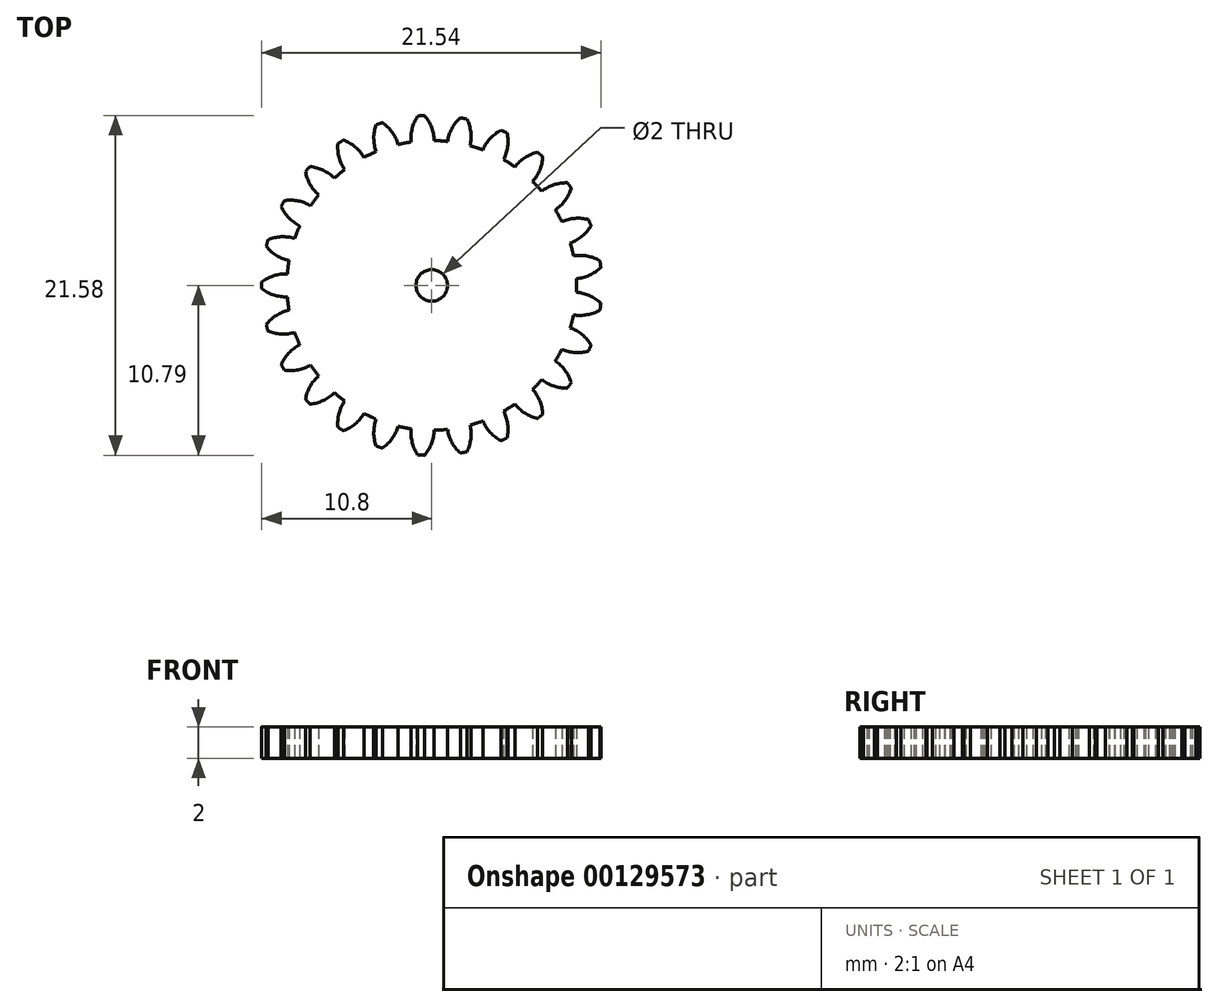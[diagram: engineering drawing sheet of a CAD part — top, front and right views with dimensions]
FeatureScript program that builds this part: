
annotation { "Feature Type Name" : "Feature", "Feature Type Description" : "" }
export const myFeature = defineFeature(function(context is Context, id is Id, definition is map)
    precondition{}
    {
        {
            var Q0;
            Q0=qCreatedBy(makeId("Top.planeOp"),FACE);
            var sketch = newSketch(context, id + "F0", { "sketchPlane" : qUnion([Q0])});
            skCircle(sketch, "E0", {"center": v(0, 0) * mm, "radius": 9.2 * mm, "construction": true});
            skCircle(sketch, "E1", {"center": v(0, 0) * mm, "radius": 10 * mm, "construction": true});
            skCircle(sketch, "E2", {"center": v(0, 0) * mm, "radius": 10.8 * mm, "construction": true});
            skLineSegment(sketch, "E3", {"start": v(0, 0) * mm, "end": v(0, 14.58) * mm, "construction": true});
            skLineSegment(sketch, "E4", {"start": v(0, 0) * mm, "end": v(-0.92, 14.56) * mm, "construction": true});
            skLineSegment(sketch, "E5", {"start": v(0, 10) * mm, "end": v(-10.54, 10) * mm, "construction": true});
            skLineSegment(sketch, "E6", {"start": v(0, 10) * mm, "end": v(-7.33, 7.33) * mm, "construction": true});
            skCircle(sketch, "E7", {"center": v(0, 10) * mm, "radius": 2.5 * mm, "construction": true});
            skCircle(sketch, "E8", {"center": v(-2.35, 9.14) * mm, "radius": 2.5 * mm, "construction": true});
            skArc(sketch, "E9", {"start": v(-4.7, 10) * mm, "mid": v(-4.75, 9.84) * mm, "end": v(-4.8, 9.68) * mm});
            skPoint(sketch, "E10.center", {"position": v(4.35, 4.65) * mm});
            skCircle(sketch, "E11", {"center": v(0, 0) * mm, "radius": 1 * mm});
            skArc(sketch, "E12", {"start": v(0.15, 9.2) * mm, "mid": v(-0.02, 10.05) * mm, "end": v(-0.47, 10.79) * mm});
            skArc(sketch, "E13.MirrorCS", {"start": v(-1.3, 9.1) * mm, "mid": v(-1.24, 9.97) * mm, "end": v(-0.89, 10.76) * mm});
            skArc(sketch, "E14", {"start": v(-0.47, 10.79) * mm, "mid": v(-0.68, 10.78) * mm, "end": v(-0.89, 10.76) * mm});
            skArc(sketch, "E15.1.0", {"start": v(-3.14, 10.33) * mm, "mid": v(-3.34, 10.27) * mm, "end": v(-3.54, 10.2) * mm});
            skArc(sketch, "E15.1.1", {"start": v(-2.14, 8.95) * mm, "mid": v(-2.52, 9.73) * mm, "end": v(-3.14, 10.33) * mm});
            skArc(sketch, "E15.1.2", {"start": v(-3.53, 8.5) * mm, "mid": v(-3.68, 9.35) * mm, "end": v(-3.54, 10.2) * mm});
            skArc(sketch, "E15.2.0", {"start": v(-5.6, 9.23) * mm, "mid": v(-5.79, 9.12) * mm, "end": v(-5.96, 9) * mm});
            skArc(sketch, "E15.2.1", {"start": v(-4.3, 8.13) * mm, "mid": v(-4.86, 8.8) * mm, "end": v(-5.6, 9.23) * mm});
            skArc(sketch, "E15.2.2", {"start": v(-5.53, 7.35) * mm, "mid": v(-5.9, 8.14) * mm, "end": v(-5.96, 9) * mm});
            skArc(sketch, "E15.3.0", {"start": v(-7.73, 7.55) * mm, "mid": v(-7.87, 7.4) * mm, "end": v(-8.02, 7.24) * mm});
            skArc(sketch, "E15.3.1", {"start": v(-6.19, 6.8) * mm, "mid": v(-6.9, 7.31) * mm, "end": v(-7.73, 7.55) * mm});
            skArc(sketch, "E15.3.2", {"start": v(-7.18, 5.75) * mm, "mid": v(-7.73, 6.42) * mm, "end": v(-8.02, 7.24) * mm});
            skArc(sketch, "E15.4.0", {"start": v(-9.36, 5.39) * mm, "mid": v(-9.46, 5.2) * mm, "end": v(-9.56, 5.02) * mm});
            skArc(sketch, "E15.4.1", {"start": v(-7.69, 5.06) * mm, "mid": v(-8.5, 5.37) * mm, "end": v(-9.36, 5.39) * mm});
            skArc(sketch, "E15.4.2", {"start": v(-8.39, 3.78) * mm, "mid": v(-9.08, 4.3) * mm, "end": v(-9.56, 5.02) * mm});
            skArc(sketch, "E15.5.0", {"start": v(-10.4, 2.9) * mm, "mid": v(-10.46, 2.69) * mm, "end": v(-10.51, 2.48) * mm});
            skArc(sketch, "E15.5.1", {"start": v(-8.7, 2.99) * mm, "mid": v(-9.56, 3.09) * mm, "end": v(-10.4, 2.9) * mm});
            skArc(sketch, "E15.5.2", {"start": v(-9.06, 1.58) * mm, "mid": v(-9.87, 1.9) * mm, "end": v(-10.51, 2.48) * mm});
            skArc(sketch, "E15.6.0", {"start": v(-10.8, 0.21) * mm, "mid": v(-10.8, 0) * mm, "end": v(-10.8, -0.21) * mm});
            skArc(sketch, "E15.6.1", {"start": v(-9.17, 0.73) * mm, "mid": v(-10.03, 0.61) * mm, "end": v(-10.8, 0.21) * mm});
            skArc(sketch, "E15.6.2", {"start": v(-9.17, -0.73) * mm, "mid": v(-10.03, -0.61) * mm, "end": v(-10.8, -0.21) * mm});
            skArc(sketch, "E15.7.0", {"start": v(-10.51, -2.48) * mm, "mid": v(-10.46, -2.69) * mm, "end": v(-10.4, -2.9) * mm});
            skArc(sketch, "E15.7.1", {"start": v(-9.06, -1.58) * mm, "mid": v(-9.87, -1.9) * mm, "end": v(-10.51, -2.48) * mm});
            skArc(sketch, "E15.7.2", {"start": v(-8.7, -2.99) * mm, "mid": v(-9.56, -3.09) * mm, "end": v(-10.4, -2.9) * mm});
            skArc(sketch, "E15.8.0", {"start": v(-9.56, -5.02) * mm, "mid": v(-9.46, -5.2) * mm, "end": v(-9.36, -5.39) * mm});
            skArc(sketch, "E15.8.1", {"start": v(-8.39, -3.78) * mm, "mid": v(-9.08, -4.3) * mm, "end": v(-9.56, -5.02) * mm});
            skArc(sketch, "E15.8.2", {"start": v(-7.69, -5.06) * mm, "mid": v(-8.5, -5.37) * mm, "end": v(-9.36, -5.39) * mm});
            skArc(sketch, "E15.9.0", {"start": v(-8.02, -7.24) * mm, "mid": v(-7.87, -7.4) * mm, "end": v(-7.73, -7.55) * mm});
            skArc(sketch, "E15.9.1", {"start": v(-7.18, -5.75) * mm, "mid": v(-7.73, -6.42) * mm, "end": v(-8.02, -7.24) * mm});
            skArc(sketch, "E15.9.2", {"start": v(-6.19, -6.8) * mm, "mid": v(-6.9, -7.31) * mm, "end": v(-7.73, -7.55) * mm});
            skArc(sketch, "E15.10.0", {"start": v(-5.96, -9) * mm, "mid": v(-5.79, -9.12) * mm, "end": v(-5.6, -9.23) * mm});
            skArc(sketch, "E15.10.1", {"start": v(-5.53, -7.35) * mm, "mid": v(-5.9, -8.14) * mm, "end": v(-5.96, -9) * mm});
            skArc(sketch, "E15.10.2", {"start": v(-4.3, -8.13) * mm, "mid": v(-4.86, -8.8) * mm, "end": v(-5.6, -9.23) * mm});
            skArc(sketch, "E15.11.0", {"start": v(-3.54, -10.2) * mm, "mid": v(-3.34, -10.27) * mm, "end": v(-3.14, -10.33) * mm});
            skArc(sketch, "E15.11.1", {"start": v(-3.53, -8.5) * mm, "mid": v(-3.68, -9.35) * mm, "end": v(-3.54, -10.2) * mm});
            skArc(sketch, "E15.11.2", {"start": v(-2.14, -8.95) * mm, "mid": v(-2.52, -9.73) * mm, "end": v(-3.14, -10.33) * mm});
            skArc(sketch, "E15.12.0", {"start": v(-0.89, -10.76) * mm, "mid": v(-0.68, -10.78) * mm, "end": v(-0.47, -10.79) * mm});
            skArc(sketch, "E15.12.1", {"start": v(-1.3, -9.1) * mm, "mid": v(-1.24, -9.97) * mm, "end": v(-0.89, -10.76) * mm});
            skArc(sketch, "E15.12.2", {"start": v(0.15, -9.2) * mm, "mid": v(-0.02, -10.05) * mm, "end": v(-0.47, -10.79) * mm});
            skArc(sketch, "E15.13.0", {"start": v(1.82, -10.65) * mm, "mid": v(2.02, -10.6) * mm, "end": v(2.23, -10.57) * mm});
            skArc(sketch, "E15.13.1", {"start": v(1, -9.15) * mm, "mid": v(1.28, -9.97) * mm, "end": v(1.82, -10.65) * mm});
            skArc(sketch, "E15.13.2", {"start": v(2.43, -8.87) * mm, "mid": v(2.48, -9.74) * mm, "end": v(2.23, -10.57) * mm});
            skArc(sketch, "E15.14.0", {"start": v(4.4, -9.86) * mm, "mid": v(4.6, -9.77) * mm, "end": v(4.79, -9.68) * mm});
            skArc(sketch, "E15.14.1", {"start": v(3.25, -8.6) * mm, "mid": v(3.72, -9.34) * mm, "end": v(4.4, -9.86) * mm});
            skArc(sketch, "E15.14.2", {"start": v(4.56, -7.99) * mm, "mid": v(4.82, -8.81) * mm, "end": v(4.79, -9.68) * mm});
            skArc(sketch, "E15.15.0", {"start": v(6.72, -8.45) * mm, "mid": v(6.88, -8.32) * mm, "end": v(7.05, -8.18) * mm});
            skArc(sketch, "E15.15.1", {"start": v(5.29, -7.53) * mm, "mid": v(5.92, -8.12) * mm, "end": v(6.72, -8.45) * mm});
            skArc(sketch, "E15.15.2", {"start": v(6.4, -6.6) * mm, "mid": v(6.87, -7.34) * mm, "end": v(7.05, -8.18) * mm});
            skArc(sketch, "E15.16.0", {"start": v(8.61, -6.52) * mm, "mid": v(8.74, -6.35) * mm, "end": v(8.86, -6.18) * mm});
            skArc(sketch, "E15.16.1", {"start": v(7, -5.98) * mm, "mid": v(7.75, -6.4) * mm, "end": v(8.61, -6.52) * mm});
            skArc(sketch, "E15.16.2", {"start": v(7.85, -4.8) * mm, "mid": v(8.47, -5.4) * mm, "end": v(8.86, -6.18) * mm});
            skArc(sketch, "E15.17.0", {"start": v(9.96, -4.17) * mm, "mid": v(10.04, -3.98) * mm, "end": v(10.12, -3.78) * mm});
            skArc(sketch, "E15.17.1", {"start": v(8.26, -4.05) * mm, "mid": v(9.1, -4.26) * mm, "end": v(9.96, -4.17) * mm});
            skArc(sketch, "E15.17.2", {"start": v(8.8, -2.7) * mm, "mid": v(9.55, -3.12) * mm, "end": v(10.12, -3.78) * mm});
            skArc(sketch, "E15.18.0", {"start": v(10.69, -1.56) * mm, "mid": v(10.71, -1.35) * mm, "end": v(10.74, -1.14) * mm});
            skArc(sketch, "E15.18.1", {"start": v(9, -1.87) * mm, "mid": v(9.87, -1.86) * mm, "end": v(10.69, -1.56) * mm});
            skArc(sketch, "E15.18.2", {"start": v(9.2, -0.43) * mm, "mid": v(10.03, -0.65) * mm, "end": v(10.74, -1.14) * mm});
            skArc(sketch, "E15.19.0", {"start": v(10.74, 1.14) * mm, "mid": v(10.71, 1.35) * mm, "end": v(10.69, 1.56) * mm});
            skArc(sketch, "E15.19.1", {"start": v(9.2, 0.43) * mm, "mid": v(10.03, 0.65) * mm, "end": v(10.74, 1.14) * mm});
            skArc(sketch, "E15.19.2", {"start": v(9, 1.87) * mm, "mid": v(9.87, 1.86) * mm, "end": v(10.69, 1.56) * mm});
            skArc(sketch, "E15.20.0", {"start": v(10.12, 3.78) * mm, "mid": v(10.04, 3.98) * mm, "end": v(9.96, 4.17) * mm});
            skArc(sketch, "E15.20.1", {"start": v(8.8, 2.7) * mm, "mid": v(9.55, 3.12) * mm, "end": v(10.12, 3.78) * mm});
            skArc(sketch, "E15.20.2", {"start": v(8.26, 4.05) * mm, "mid": v(9.1, 4.26) * mm, "end": v(9.96, 4.17) * mm});
            skArc(sketch, "E15.21.0", {"start": v(8.86, 6.18) * mm, "mid": v(8.74, 6.35) * mm, "end": v(8.61, 6.52) * mm});
            skArc(sketch, "E15.21.1", {"start": v(7.85, 4.8) * mm, "mid": v(8.47, 5.4) * mm, "end": v(8.86, 6.18) * mm});
            skArc(sketch, "E15.21.2", {"start": v(7, 5.98) * mm, "mid": v(7.75, 6.4) * mm, "end": v(8.61, 6.52) * mm});
            skArc(sketch, "E15.22.0", {"start": v(7.05, 8.18) * mm, "mid": v(6.88, 8.32) * mm, "end": v(6.72, 8.45) * mm});
            skArc(sketch, "E15.22.1", {"start": v(6.4, 6.6) * mm, "mid": v(6.87, 7.34) * mm, "end": v(7.05, 8.18) * mm});
            skArc(sketch, "E15.22.2", {"start": v(5.29, 7.53) * mm, "mid": v(5.92, 8.12) * mm, "end": v(6.72, 8.45) * mm});
            skArc(sketch, "E15.23.0", {"start": v(4.79, 9.68) * mm, "mid": v(4.6, 9.77) * mm, "end": v(4.4, 9.86) * mm});
            skArc(sketch, "E15.23.1", {"start": v(4.56, 7.99) * mm, "mid": v(4.82, 8.81) * mm, "end": v(4.79, 9.68) * mm});
            skArc(sketch, "E15.23.2", {"start": v(3.25, 8.6) * mm, "mid": v(3.72, 9.34) * mm, "end": v(4.4, 9.86) * mm});
            skArc(sketch, "E15.24.0", {"start": v(2.23, 10.57) * mm, "mid": v(2.02, 10.6) * mm, "end": v(1.82, 10.65) * mm});
            skArc(sketch, "E15.24.1", {"start": v(2.43, 8.87) * mm, "mid": v(2.48, 9.74) * mm, "end": v(2.23, 10.57) * mm});
            skArc(sketch, "E15.24.2", {"start": v(1, 9.15) * mm, "mid": v(1.28, 9.97) * mm, "end": v(1.82, 10.65) * mm});
            skArc(sketch, "E16", {"start": v(1, 9.15) * mm, "mid": v(0.58, 9.18) * mm, "end": v(0.15, 9.2) * mm});
            skArc(sketch, "E17.1.0", {"start": v(-1.3, 9.1) * mm, "mid": v(-1.72, 9.04) * mm, "end": v(-2.14, 8.95) * mm});
            skArc(sketch, "E17.2.0", {"start": v(-3.53, 8.5) * mm, "mid": v(-3.92, 8.32) * mm, "end": v(-4.3, 8.13) * mm});
            skArc(sketch, "E17.3.0", {"start": v(-5.53, 7.35) * mm, "mid": v(-5.86, 7.09) * mm, "end": v(-6.19, 6.8) * mm});
            skArc(sketch, "E17.4.0", {"start": v(-7.18, 5.75) * mm, "mid": v(-7.44, 5.4) * mm, "end": v(-7.69, 5.06) * mm});
            skArc(sketch, "E17.5.0", {"start": v(-8.39, 3.78) * mm, "mid": v(-8.55, 3.39) * mm, "end": v(-8.7, 2.99) * mm});
            skArc(sketch, "E17.6.0", {"start": v(-9.06, 1.58) * mm, "mid": v(-9.13, 1.15) * mm, "end": v(-9.17, 0.73) * mm});
            skArc(sketch, "E17.7.0", {"start": v(-9.17, -0.73) * mm, "mid": v(-9.13, -1.15) * mm, "end": v(-9.06, -1.58) * mm});
            skArc(sketch, "E17.8.0", {"start": v(-8.7, -2.99) * mm, "mid": v(-8.55, -3.39) * mm, "end": v(-8.39, -3.78) * mm});
            skArc(sketch, "E17.9.0", {"start": v(-7.69, -5.06) * mm, "mid": v(-7.44, -5.4) * mm, "end": v(-7.18, -5.75) * mm});
            skArc(sketch, "E17.10.0", {"start": v(-6.19, -6.8) * mm, "mid": v(-5.86, -7.09) * mm, "end": v(-5.53, -7.35) * mm});
            skArc(sketch, "E17.11.0", {"start": v(-4.3, -8.13) * mm, "mid": v(-3.92, -8.32) * mm, "end": v(-3.53, -8.5) * mm});
            skArc(sketch, "E17.12.0", {"start": v(-2.14, -8.95) * mm, "mid": v(-1.72, -9.04) * mm, "end": v(-1.3, -9.1) * mm});
            skArc(sketch, "E17.13.0", {"start": v(0.15, -9.2) * mm, "mid": v(0.58, -9.18) * mm, "end": v(1, -9.15) * mm});
            skArc(sketch, "E17.14.0", {"start": v(2.43, -8.87) * mm, "mid": v(2.84, -8.75) * mm, "end": v(3.25, -8.6) * mm});
            skArc(sketch, "E17.15.0", {"start": v(4.56, -7.99) * mm, "mid": v(4.93, -7.77) * mm, "end": v(5.29, -7.53) * mm});
            skArc(sketch, "E17.16.0", {"start": v(6.4, -6.6) * mm, "mid": v(6.7, -6.3) * mm, "end": v(7, -5.98) * mm});
            skArc(sketch, "E17.17.0", {"start": v(7.85, -4.8) * mm, "mid": v(8.06, -4.43) * mm, "end": v(8.26, -4.05) * mm});
            skArc(sketch, "E17.18.0", {"start": v(8.8, -2.7) * mm, "mid": v(8.91, -2.29) * mm, "end": v(9, -1.87) * mm});
            skArc(sketch, "E17.19.0", {"start": v(9.2, -0.43) * mm, "mid": v(9.2, 0) * mm, "end": v(9.2, 0.43) * mm});
            skArc(sketch, "E17.20.0", {"start": v(9, 1.87) * mm, "mid": v(8.91, 2.29) * mm, "end": v(8.8, 2.7) * mm});
            skArc(sketch, "E17.21.0", {"start": v(8.26, 4.05) * mm, "mid": v(8.06, 4.43) * mm, "end": v(7.85, 4.8) * mm});
            skArc(sketch, "E17.22.0", {"start": v(7, 5.98) * mm, "mid": v(6.7, 6.3) * mm, "end": v(6.4, 6.6) * mm});
            skArc(sketch, "E17.23.0", {"start": v(5.29, 7.53) * mm, "mid": v(4.93, 7.77) * mm, "end": v(4.56, 7.99) * mm});
            skArc(sketch, "E17.24.0", {"start": v(3.25, 8.6) * mm, "mid": v(2.84, 8.75) * mm, "end": v(2.43, 8.87) * mm});
            skSolve(sketch);
        }
        {
            var Q0;
            Q0=makeQuery(id+"F0.imprint","IMPRINT",FACE,{"disambiguationData":[TD([[makeQuery(id+"F0.imprint","IMPRINT",EDGE,{"derivedFrom":sQuery(id+"F0.wireOp",EDGE,"E11")}),-1.0]])]});
            extrude(context, id + "F1", {"entities" : qUnion([Q0]), "depth" : 2 * mm});
        }
    });
